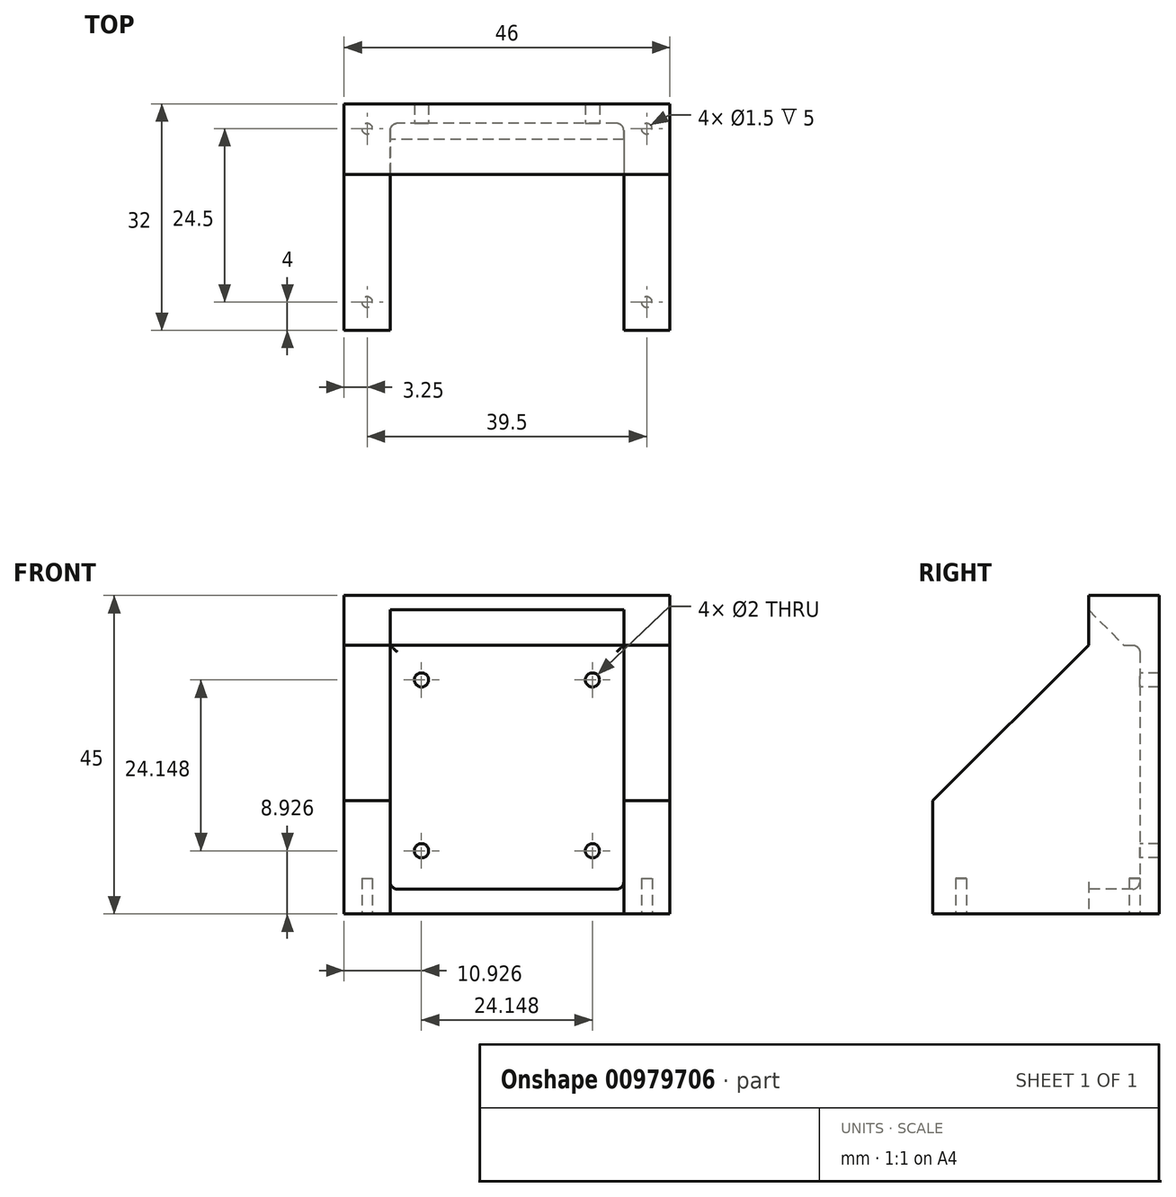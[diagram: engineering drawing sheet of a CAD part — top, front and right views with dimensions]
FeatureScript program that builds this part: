
annotation { "Feature Type Name" : "Feature", "Feature Type Description" : "" }
export const myFeature = defineFeature(function(context is Context, id is Id, definition is map)
    precondition{}
    {
        {
            var Q0;
            Q0=qCreatedBy(makeId("Right.planeOp"),FACE);
            var sketch = newSketch(context, id + "F0", { "sketchPlane" : qUnion([Q0])});
            skLineSegment(sketch, "E0.bottom", {"start": v(0, 0) * mm, "end": v(32, 0) * mm});
            skLineSegment(sketch, "E0.top", {"start": v(0, 42) * mm, "end": v(32, 42) * mm});
            skLineSegment(sketch, "E0.left", {"start": v(0, 0) * mm, "end": v(0, 42) * mm});
            skLineSegment(sketch, "E0.right", {"start": v(32, 0) * mm, "end": v(32, 42) * mm});
            skSolve(sketch);
        }
        {
            var Q0;
            Q0=makeQuery(id+"F0.imprint","IMPRINT",FACE,{"disambiguationData":[TD([[makeQuery(id+"F0.imprint","IMPRINT",EDGE,{"derivedFrom":sQuery(id+"F0.wireOp",EDGE,"E0.bottom")}),1.0]])]});
            extrude(context, id + "F1", {"entities" : qUnion([Q0]), "oppositeDirection" : true, "depth" : 46 * mm, "offsetDistance" : 25 * mm});
        }
        {
            var Q0;
            Q0=qCreatedBy(makeId("Top.planeOp"),FACE);
            var sketch = newSketch(context, id + "F2", { "sketchPlane" : qUnion([Q0])});
            skLineSegment(sketch, "E1.bottom", {"start": v(-39.5, 0) * mm, "end": v(-6.5, 0) * mm});
            skLineSegment(sketch, "E1.top", {"start": v(-39.5, 29.25) * mm, "end": v(-6.5, 29.25) * mm});
            skLineSegment(sketch, "E1.left", {"start": v(-39.5, 0) * mm, "end": v(-39.5, 29.25) * mm});
            skLineSegment(sketch, "E1.right", {"start": v(-6.5, 0) * mm, "end": v(-6.5, 29.25) * mm});
            skSolve(sketch);
        }
        {
            var Q0;
            Q0 = qSketchRegion(id + "F2", true);
            extrude(context, id + "F3", {"entities" : qUnion([Q0]), "operationType" : NewBodyOperationType.REMOVE, "endBound" : BoundingType.THROUGH_ALL, "depth" : 25 * mm, "offsetDistance" : 25 * mm});
        }
        {
            var Q0;
            {var subQ0=sQuery(id+"F0.wireOp",EDGE,"E0.left");var subQ1=sQuery(id+"F0.wireOp",EDGE,"E0.top");Q0=makeQuery(id+"F3.boolean.opBoolean","SPLIT",EDGE,{"disambiguationData":[TD([makeQuery(id+"F3.opExtrude","SWEPT_FACE",FACE,{"disambiguationData":[OSD([sQuery(id+"F2.wireOp",EDGE,"E1.left")])]})])],"derivedFrom":makeQuery(id+"F1.opExtrude","SWEPT_EDGE",EDGE,{"disambiguationData":[OSD([subQ1,subQ0])]})});}
            var Q1;
            {var subQ0=sQuery(id+"F0.wireOp",EDGE,"E0.left");var subQ1=sQuery(id+"F0.wireOp",EDGE,"E0.top");Q1=makeQuery(id+"F3.boolean.opBoolean","SPLIT",EDGE,{"disambiguationData":[TD([makeQuery(id+"F3.opExtrude","SWEPT_FACE",FACE,{"disambiguationData":[OSD([sQuery(id+"F2.wireOp",EDGE,"E1.right")])]})])],"derivedFrom":makeQuery(id+"F1.opExtrude","SWEPT_EDGE",EDGE,{"disambiguationData":[OSD([subQ1,subQ0])]})});}
            chamfer(context, id + "F4", {"entities" : qUnion([Q0, Q1]), "width" : 26 * mm, "tangentPropagation" : true});
        }
        {
            var Q0;
            Q0=makeQuery(id+"F3.boolean.opBoolean","COPY",FACE,{"derivedFrom":makeQuery(id+"F3.opExtrude","SWEPT_FACE",FACE,{"disambiguationData":[OSD([sQuery(id+"F2.wireOp",EDGE,"E1.top")])]})});
            var sketch = newSketch(context, id + "F5", { "sketchPlane" : qUnion([Q0])});
            skPoint(sketch, "E2", {"position": v(-23, 21) * mm});
            skCircle(sketch, "E3", {"center": v(-23, 21) * mm, "radius": 17.07 * mm, "construction": true});
            skLineSegment(sketch, "E4", {"start": v(-35.07, 33.07) * mm, "end": v(-10.93, 8.93) * mm, "construction": true});
            skLineSegment(sketch, "E5", {"start": v(-35.07, 8.93) * mm, "end": v(-10.93, 33.07) * mm, "construction": true});
            skCircle(sketch, "E6", {"center": v(-35.07, 33.07) * mm, "radius": 1 * mm});
            skCircle(sketch, "E7", {"center": v(-10.93, 33.07) * mm, "radius": 1 * mm});
            skCircle(sketch, "E8", {"center": v(-35.07, 8.93) * mm, "radius": 1 * mm});
            skCircle(sketch, "E9", {"center": v(-10.93, 8.93) * mm, "radius": 1 * mm});
            skSolve(sketch);
        }
        {
            var Q0;
            Q0 = qSketchRegion(id + "F5", true);
            extrude(context, id + "F6", {"entities" : qUnion([Q0]), "operationType" : NewBodyOperationType.REMOVE, "oppositeDirection" : true, "depth" : 25 * mm, "offsetDistance" : 25 * mm});
        }
        {
            var Q0;
            Q0=makeQuery(id+"F1.opExtrude","SWEPT_FACE",FACE,{"disambiguationData":[OSD([sQuery(id+"F0.wireOp",EDGE,"E0.right")])]});
            var sketch = newSketch(context, id + "F7", { "sketchPlane" : qUnion([Q0])});
            skLineSegment(sketch, "E10.bottom", {"start": v(46, 45) * mm, "end": v(0, 45) * mm});
            skLineSegment(sketch, "E10.top", {"start": v(46, 38) * mm, "end": v(0, 38) * mm});
            skLineSegment(sketch, "E10.left", {"start": v(0, 45) * mm, "end": v(0, 38) * mm});
            skLineSegment(sketch, "E10.right", {"start": v(46, 45) * mm, "end": v(46, 38) * mm});
            skLineSegment(sketch, "E11.bottom", {"start": v(0, 0) * mm, "end": v(46, 0) * mm});
            skLineSegment(sketch, "E11.top", {"start": v(0, 3.5) * mm, "end": v(46, 3.5) * mm});
            skLineSegment(sketch, "E11.left", {"start": v(0, 0) * mm, "end": v(0, 3.5) * mm});
            skLineSegment(sketch, "E11.right", {"start": v(46, 0) * mm, "end": v(46, 3.5) * mm});
            skSolve(sketch);
        }
        {
            var Q0;
            Q0 = qSketchRegion(id + "F7", true);
            extrude(context, id + "F8", {"entities" : qUnion([Q0]), "operationType" : NewBodyOperationType.ADD, "oppositeDirection" : true, "depth" : 10 * mm, "offsetDistance" : 25 * mm});
        }
        {
            var Q0;
            {var subQ0=sQuery(id+"F0.wireOp",EDGE,"E0.left");var subQ1=sQuery(id+"F0.wireOp",EDGE,"E0.top");var subQ2=sQuery(id+"F7.wireOp",EDGE,"E10.top");Q0=makeQuery(id+"F8.boolean.opBoolean","SPLIT",EDGE,{"disambiguationData":[topologyDisambiguationEdgeConnected([makeQuery(id+"F4.opChamfer","BLEND_FACE",FACE,{"disambiguationData":[OSD([subQ1,subQ0]),TDD([makeQuery(id+"F3.boolean.opBoolean","SPLIT",EDGE,{"disambiguationData":[TD([makeQuery(id+"F3.opExtrude","SWEPT_FACE",FACE,{"disambiguationData":[OSD([sQuery(id+"F2.wireOp",EDGE,"E1.left")])]})])],"derivedFrom":makeQuery(id+"F1.opExtrude","SWEPT_EDGE",EDGE,{"disambiguationData":[OSD([subQ1,subQ0])]})})])]})])],"derivedFrom":makeQuery(id+"F8.opExtrude","CAP_EDGE",EDGE,{"disambiguationData":[OSD([subQ2])],"isStart":false})});}
            var Q1;
            {var subQ0=sQuery(id+"F0.wireOp",EDGE,"E0.left");var subQ1=sQuery(id+"F0.wireOp",EDGE,"E0.top");var subQ2=sQuery(id+"F7.wireOp",EDGE,"E10.top");Q1=makeQuery(id+"F8.boolean.opBoolean","SPLIT",EDGE,{"disambiguationData":[topologyDisambiguationEdgeConnected([makeQuery(id+"F4.opChamfer","BLEND_FACE",FACE,{"disambiguationData":[OSD([subQ1,subQ0]),TDD([makeQuery(id+"F3.boolean.opBoolean","SPLIT",EDGE,{"disambiguationData":[TD([makeQuery(id+"F3.opExtrude","SWEPT_FACE",FACE,{"disambiguationData":[OSD([sQuery(id+"F2.wireOp",EDGE,"E1.right")])]})])],"derivedFrom":makeQuery(id+"F1.opExtrude","SWEPT_EDGE",EDGE,{"disambiguationData":[OSD([subQ1,subQ0])]})})])]})])],"derivedFrom":makeQuery(id+"F8.opExtrude","CAP_EDGE",EDGE,{"disambiguationData":[OSD([subQ2])],"isStart":false})});}
            chamfer(context, id + "F9", {"entities" : qUnion([Q0, Q1]), "width" : 5 * mm, "tangentPropagation" : true});
        }
        {
            var Q0;
            Q0=makeQuery(id+"F3.boolean.opBoolean","COPY",EDGE,{"derivedFrom":makeQuery(id+"F3.opExtrude","SWEPT_EDGE",EDGE,{"disambiguationData":[OSD([sQuery(id+"F2.wireOp",EDGE,"E1.top"),sQuery(id+"F2.wireOp",EDGE,"E1.left")])]})});
            var Q1;
            Q1=makeQuery(id+"F3.boolean.opBoolean","COPY",EDGE,{"derivedFrom":makeQuery(id+"F3.opExtrude","SWEPT_EDGE",EDGE,{"disambiguationData":[OSD([sQuery(id+"F2.wireOp",EDGE,"E1.top"),sQuery(id+"F2.wireOp",EDGE,"E1.right")])]})});
            var Q2;
            Q2=makeQuery(id+"F8.boolean.opBoolean","INTERSECT",EDGE,{"derivedFrom":[makeQuery(id+"F3.boolean.opBoolean","COPY",FACE,{"derivedFrom":makeQuery(id+"F3.opExtrude","SWEPT_FACE",FACE,{"disambiguationData":[OSD([sQuery(id+"F2.wireOp",EDGE,"E1.top")])]})}),makeQuery(id+"F8.opExtrude","SWEPT_FACE",FACE,{"disambiguationData":[OSD([sQuery(id+"F7.wireOp",EDGE,"E10.top")])]})]});
            var Q3;
            Q3=makeQuery(id+"F8.boolean.opBoolean","INTERSECT",EDGE,{"derivedFrom":[makeQuery(id+"F3.boolean.opBoolean","COPY",FACE,{"derivedFrom":makeQuery(id+"F3.opExtrude","SWEPT_FACE",FACE,{"disambiguationData":[OSD([sQuery(id+"F2.wireOp",EDGE,"E1.top")])]})}),makeQuery(id+"F8.opExtrude","SWEPT_FACE",FACE,{"disambiguationData":[OSD([sQuery(id+"F7.wireOp",EDGE,"E11.top")])]})]});
            var Q4;
            Q4=makeQuery(id+"F8.boolean.opBoolean","INTERSECT",EDGE,{"derivedFrom":[makeQuery(id+"F3.boolean.opBoolean","COPY",FACE,{"derivedFrom":makeQuery(id+"F3.opExtrude","SWEPT_FACE",FACE,{"disambiguationData":[OSD([sQuery(id+"F2.wireOp",EDGE,"E1.left")])]})}),makeQuery(id+"F8.opExtrude","SWEPT_FACE",FACE,{"disambiguationData":[OSD([sQuery(id+"F7.wireOp",EDGE,"E11.top")])]})]});
            var Q5;
            Q5=makeQuery(id+"F8.boolean.opBoolean","INTERSECT",EDGE,{"derivedFrom":[makeQuery(id+"F3.boolean.opBoolean","COPY",FACE,{"derivedFrom":makeQuery(id+"F3.opExtrude","SWEPT_FACE",FACE,{"disambiguationData":[OSD([sQuery(id+"F2.wireOp",EDGE,"E1.right")])]})}),makeQuery(id+"F8.opExtrude","SWEPT_FACE",FACE,{"disambiguationData":[OSD([sQuery(id+"F7.wireOp",EDGE,"E11.top")])]})]});
            fillet(context, id + "F10", {"entities" : qUnion([Q0, Q1, Q2, Q3, Q4, Q5]), "tangentPropagation" : true, "radius" : 1 * mm, "defaultsChanged" : false, "vertexSettings" : [], "allowEdgeOverflow" : false});
        }
        {
            var Q0;
            Q0=makeQuery(id+"F8.boolean.opBoolean","MERGE",FACE,{"derivedFrom":[makeQuery(id+"F1.opExtrude","SWEPT_FACE",FACE,{"disambiguationData":[OSD([sQuery(id+"F0.wireOp",EDGE,"E0.bottom")])]}),makeQuery(id+"F8.opExtrude","SWEPT_FACE",FACE,{"disambiguationData":[OSD([sQuery(id+"F7.wireOp",EDGE,"E11.bottom")])]})]});
            var sketch = newSketch(context, id + "F11", { "sketchPlane" : qUnion([Q0])});
            skCircle(sketch, "E12", {"center": v(-42.75, -4) * mm, "radius": 0.75 * mm});
            skCircle(sketch, "E13", {"center": v(-42.75, -28.5) * mm, "radius": 0.75 * mm});
            skCircle(sketch, "E14", {"center": v(-3.25, -28.5) * mm, "radius": 0.75 * mm});
            skCircle(sketch, "E15", {"center": v(-3.25, -4) * mm, "radius": 0.75 * mm});
            skSolve(sketch);
        }
        {
            var Q0;
            Q0 = qSketchRegion(id + "F11", true);
            extrude(context, id + "F12", {"entities" : qUnion([Q0]), "operationType" : NewBodyOperationType.REMOVE, "oppositeDirection" : true, "depth" : 5 * mm, "offsetDistance" : 25 * mm});
        }
    });
